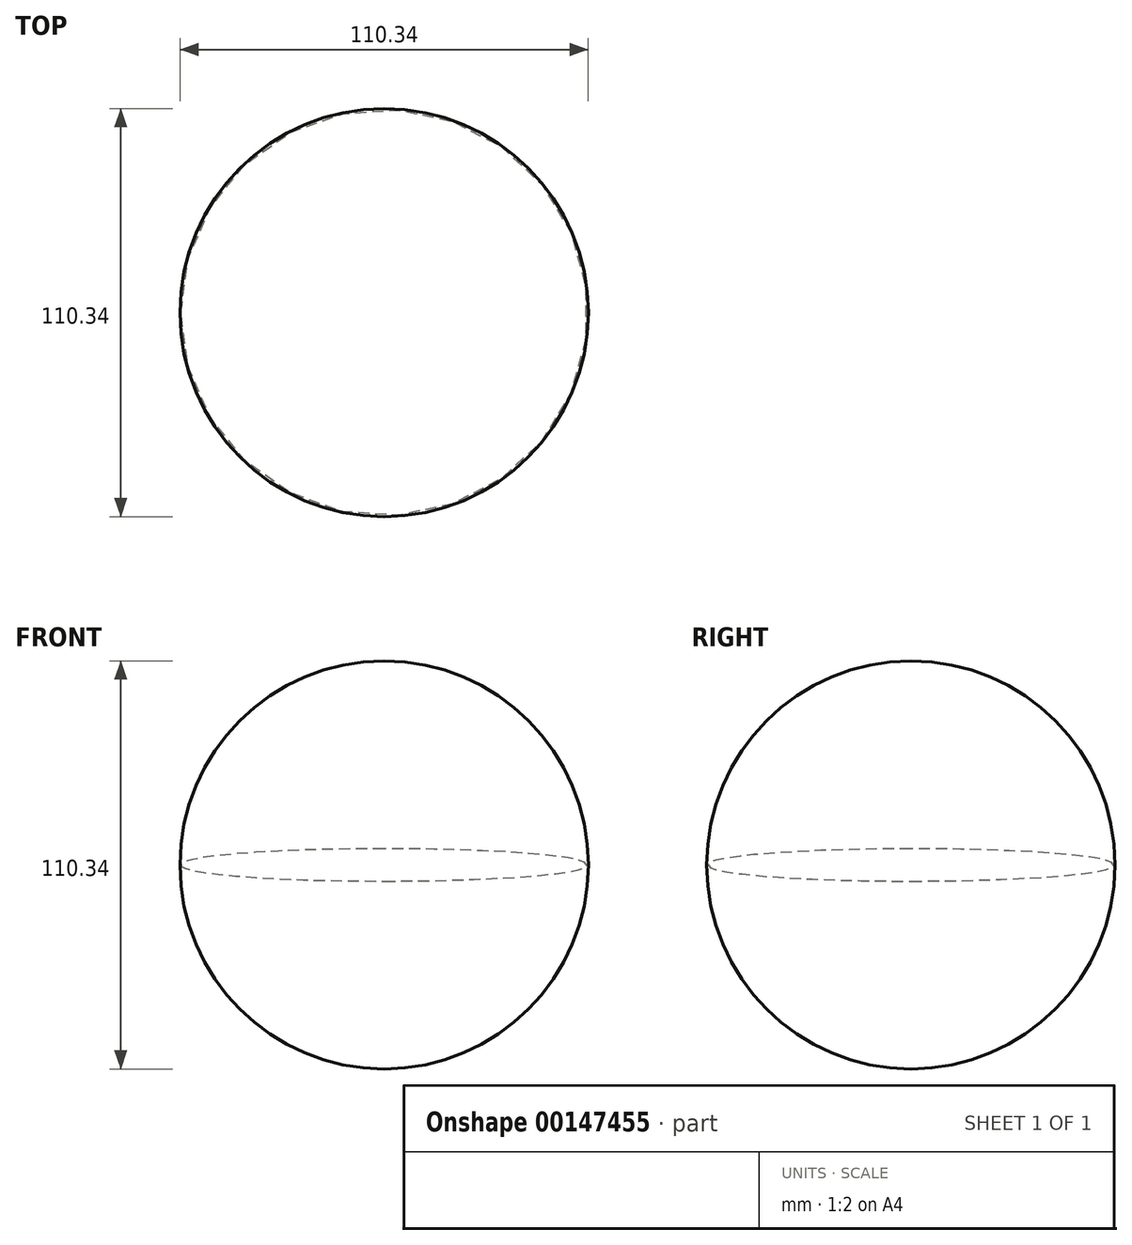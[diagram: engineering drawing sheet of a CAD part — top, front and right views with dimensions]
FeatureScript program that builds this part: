
annotation { "Feature Type Name" : "Feature", "Feature Type Description" : "" }
export const myFeature = defineFeature(function(context is Context, id is Id, definition is map)
    precondition{}
    {
        {
            var Q0;
            Q0=qCreatedBy(makeId("Front.planeOp"),FACE);
            var sketch = newSketch(context, id + "F0", { "sketchPlane" : qUnion([Q0])});
            skCircle(sketch, "E0", {"center": v(0, 0) * mm, "radius": 55.17 * mm});
            skEllipse(sketch, "E1", {"center": v(0, 0) * mm, "majorRadius": 54.96 * mm, "minorRadius": 4.39 * mm, "majorAxis": v(1, 0)});
            skLineSegment(sketch, "E2", {"start": v(0, 55.17) * mm, "end": v(0, -55.17) * mm});
            skSolve(sketch);
        }
        {
            var Q0;
            {var subQ0=sQuery(id+"F0.wireOp",EDGE,"E2");var subQ1=sQuery(id+"F0.wireOp",EDGE,"E0");var subQ2=makeQuery(id+"F0.imprint","INTERSECT",VERTEX,{"disambiguationData":[OD(0.0)],"derivedFrom":[subQ1,subQ0]});Q0=makeQuery(id+"F0.imprint","IMPRINT",FACE,{"disambiguationData":[TD([[makeQuery(id+"F0.imprint","IMPRINT",EDGE,{"disambiguationData":[TD([[subQ2,-1.0]])],"derivedFrom":subQ1}),1.0]])]});}
            var Q1;
            Q1=sQuery(id+"F0.wireOp",EDGE,"E2");
            revolve(context, id + "F1", {"entities" : qUnion([Q0]), "axis" : qUnion([Q1]), "revolveType" : RevolveType.FULL});
        }
    });
